# Revit family: 3459A_NX_Ceiling_Mount_Occupancy_Sensor
name_source: partatom
category: Communication Devices
units: mm (PartAtom-declared; Revit-internal decimal feet)

## family parameters
Cut with Voids When Loaded = No
Host = Face
Maintain Annotation Orientation = No
OmniClass Number = 23.85.80.11.27
OmniClass Title = Lighting Controls
Part Type = Normal
Room Calculation Point = No
Round Connector Dimension = Use Diameter
Shared = Yes

## types (1)
- 3459A_NX_Ceiling_Mount_Occupancy_Sensor
    Assembly Code = D5090
    Certifications = UL and cUL listed
    Coverage = 500 - 2000 sq ft, based on model
    Default Elevation = 48 "
    Description = key component in a NX Network Lighting Control System, providing programmable switching and dimming control of the projects lighting circuits
    Features = • IntelliDAPT self-adaptive technology – no manual adjustment required
• Occupancy or vacancy operation selectable per load when used with the
NX Room Controller
• All-digital sensor
• Non-volatile memory for sensor settings
• 500 to 2,000 square-foot coverage area (based on model)
• Plug and play integration with NX Room Controller
    Housing Material = Paint -  Matte White
    Manufacturer = NX Lighting Controls
    Model = NX Ceiling Mount Occupancy Sensors employ Passive Infrared
and Ultrasonic sensing technologies to turn lighting on and off based
on occupancy
    Power Requirements = Powered by NX Room Controller using plenum rated CAT5 cables (ordered separately)
    Sensing Element = Metal-Nickel
    Type Comments = Area Controller
    URL = https://www.currentlighting.com
    Warranty = 5-Years Warranty

## geometry (parser evidence)
native form markers: Sweep x2
no freeform markers — native parametric forms only
